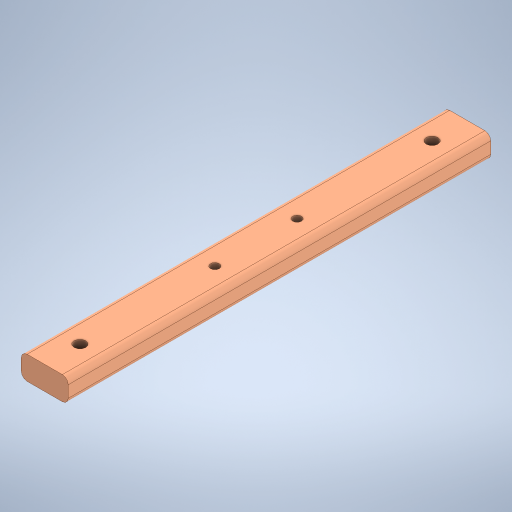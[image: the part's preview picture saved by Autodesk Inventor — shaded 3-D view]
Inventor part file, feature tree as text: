
AUTODESK INVENTOR PART (.ipt)
format: ipt  version: 2024 (Build 280153000, 153)  size: 267,776 bytes
history: native  units: mm
features: extrude x2
ambient origin geometry x8: Origin, YZ Plane, XZ Plane, XY Plane, X Axis, Y Axis, Z Axis, Center Point
bodies: Solid1 (feature_tree)
feature tree (2):
  extrude  "Extrusion1"  Depth=50.8mm
  extrude  "Extrusion2"  Depth=101.6mm
